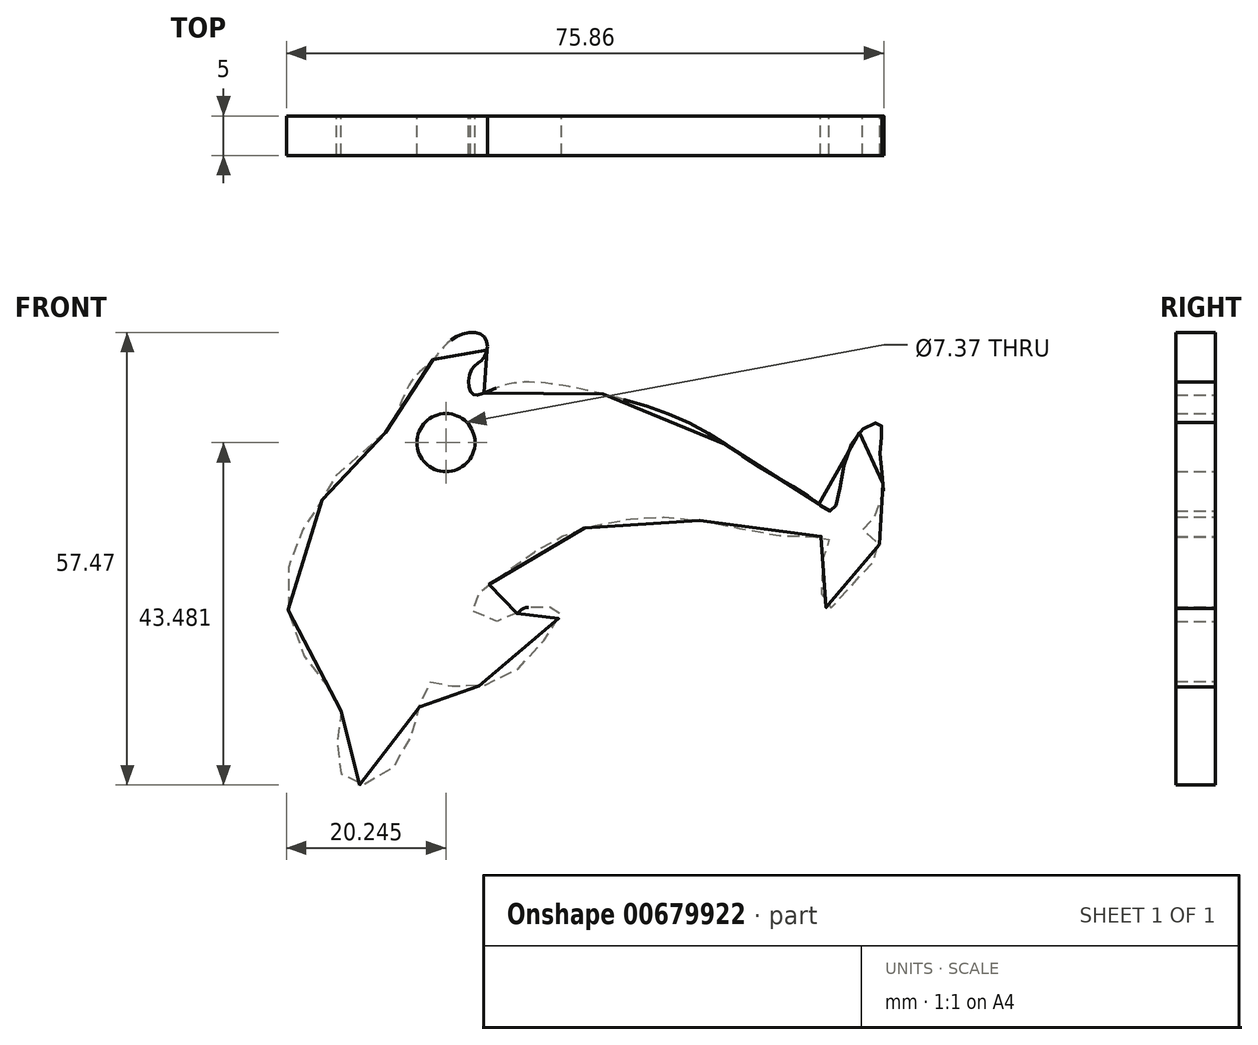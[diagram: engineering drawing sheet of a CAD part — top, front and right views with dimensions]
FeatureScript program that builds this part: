
annotation { "Feature Type Name" : "Feature", "Feature Type Description" : "" }
export const myFeature = defineFeature(function(context is Context, id is Id, definition is map)
    precondition{}
    {
        {
            var Q0;
            Q0=qCreatedBy(makeId("Front.planeOp"),FACE);
            var sketch = newSketch(context, id + "F0", { "sketchPlane" : qUnion([Q0])});
            skPoint(sketch, "E0.25.internal.snap0", {"position": v(-27.22, 6.16) * mm});
            skFitSpline(sketch, "E0", {"points": [v(-15.07, 22.34) * mm, v(-20.5, 17.85) * mm, v(-23.3, 13.55) * mm, v(-27.22, 6.16) * mm, v(-25.54, -5.89) * mm, v(-20.86, -12.43) * mm, v(-21.24, -17.3) * mm, v(-19.74, -22.17) * mm, v(-14.32, -20.47) * mm, v(-10.96, -13.37) * mm, v(-9.46, -9.44) * mm, v(-7.03, -9.81) * mm, v(0, -8.88) * mm, v(5.87, -2.9) * mm, v(7.18, 0) * mm, v(4.37, 0) * mm, v(2.5, 0) * mm, v(0, -1.59) * mm, v(-4.23, 0) * mm, v(0, 4.4) * mm, v(6.8, 8.88) * mm, v(15.78, 11.3) * mm, v(24.94, 11.12) * mm, v(36.9, 9.07) * mm, v(41.2, 8.88) * mm, v(40.45, 6.16) * mm, v(41.01, 0) * mm, v(44.75, 3.65) * mm, v(47.74, 7.94) * mm, v(45.5, 10) * mm, v(47.74, 12.43) * mm, v(47.74, 19.72) * mm, v(47.74, 23.46) * mm, v(44.2, 21.03) * mm, v(41.76, 12.43) * mm, v(39.33, 13.74) * mm, v(32.23, 18.04) * mm, v(23.63, 23.46) * mm, v(10.92, 27.57) * mm, v(0, 28.32) * mm, v(-4.04, 27.2) * mm, v(-4.23, 30.2) * mm, v(-2.54, 31.87) * mm, v(-2.54, 34.5) * mm, v(-6.1, 34.5) * mm, v(-9.46, 31.13) * mm, v(-11.9, 28.7) * mm, v(-15.07, 22.34) * mm]});
            skCircle(sketch, "E1", {"center": v(-7.4, 21.03) * mm, "radius": 3.69 * mm});
            skSolve(sketch);
        }
        {
            var Q0;
            Q0=makeQuery(id+"F0.imprint","IMPRINT",FACE,{"disambiguationData":[TD([[makeQuery(id+"F0.imprint","IMPRINT",EDGE,{"derivedFrom":sQuery(id+"F0.wireOp",EDGE,"E0")}),1.0]])]});
            var Q1;
            Q1=sQuery(id+"F0.wireOp",EDGE,"E0");
            extrude(context, id + "F1", {"entities" : qUnion([Q0]), "surfaceEntities" : qUnion([Q1]), "depth" : 5 * mm, "offsetDistance" : 25.4 * mm});
        }
    });
